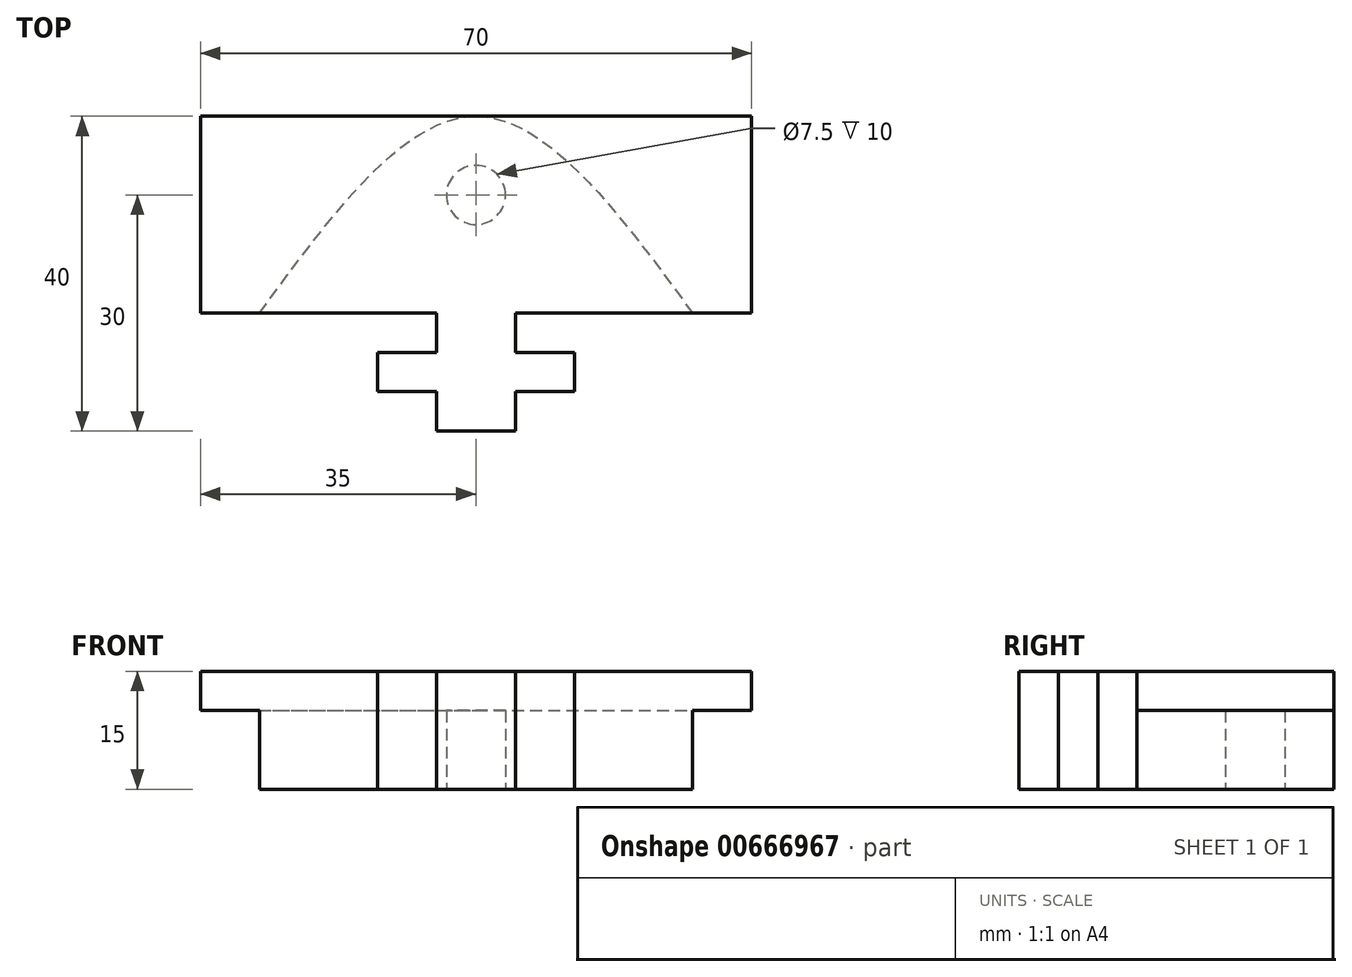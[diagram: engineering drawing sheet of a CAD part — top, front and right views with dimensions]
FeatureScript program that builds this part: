
annotation { "Feature Type Name" : "Feature", "Feature Type Description" : "" }
export const myFeature = defineFeature(function(context is Context, id is Id, definition is map)
    precondition{}
    {
        {
            var Q0;
            Q0=qCreatedBy(makeId("Top.planeOp"),FACE);
            var sketch = newSketch(context, id + "F0", { "sketchPlane" : qUnion([Q0])});
            skLineSegment(sketch, "E0.bottom", {"start": v(-35, 12.5) * mm, "end": v(35, 12.5) * mm});
            skLineSegment(sketch, "E0.top", {"start": v(-35, -12.5) * mm, "end": v(-5, -12.5) * mm});
            skLineSegment(sketch, "E0.left", {"start": v(-35, 12.5) * mm, "end": v(-35, -12.5) * mm});
            skLineSegment(sketch, "E0.right", {"start": v(35, 12.5) * mm, "end": v(35, -12.5) * mm});
            skPoint(sketch, "E0.middle", {"position": v(0, 0) * mm});
            skLineSegment(sketch, "E1", {"start": v(0, -27.5) * mm, "end": v(0, -58.53) * mm, "construction": true});
            skLineSegment(sketch, "E2", {"start": v(-5, -12.5) * mm, "end": v(-5, -17.5) * mm});
            skLineSegment(sketch, "E3", {"start": v(-5, -17.5) * mm, "end": v(-12.5, -17.5) * mm});
            skLineSegment(sketch, "E4", {"start": v(-12.5, -17.5) * mm, "end": v(-12.5, -22.5) * mm});
            skLineSegment(sketch, "E5", {"start": v(-12.5, -22.5) * mm, "end": v(-5, -22.5) * mm});
            skLineSegment(sketch, "E6", {"start": v(-5, -22.5) * mm, "end": v(-5, -27.5) * mm});
            skLineSegment(sketch, "E7", {"start": v(-5, -27.5) * mm, "end": v(0, -27.5) * mm});
            skLineSegment(sketch, "E8.MirrorCS", {"start": v(5, -17.5) * mm, "end": v(12.5, -17.5) * mm});
            skLineSegment(sketch, "E9.MirrorCS", {"start": v(5, -12.5) * mm, "end": v(5, -17.5) * mm});
            skLineSegment(sketch, "E10.MirrorCS", {"start": v(12.5, -17.5) * mm, "end": v(12.5, -22.5) * mm});
            skLineSegment(sketch, "E11.MirrorCS", {"start": v(12.5, -22.5) * mm, "end": v(5, -22.5) * mm});
            skLineSegment(sketch, "E12.MirrorCS", {"start": v(5, -22.5) * mm, "end": v(5, -27.5) * mm});
            skLineSegment(sketch, "E13.MirrorCS", {"start": v(5, -27.5) * mm, "end": v(0, -27.5) * mm});
            skLineSegment(sketch, "E14.trimOffspring", {"start": v(5, -12.5) * mm, "end": v(35, -12.5) * mm});
            skLineSegment(sketch, "E15", {"start": v(0, 12.5) * mm, "end": v(0, -27.5) * mm, "construction": true});
            skPoint(sketch, "E16", {"position": v(0, 2.5) * mm});
            skPoint(sketch, "E17", {"position": v(-27.5, -12.5) * mm});
            skPoint(sketch, "E18", {"position": v(27.5, -12.5) * mm});
            skFitSpline(sketch, "E19", {"points": [v(-27.5, -12.5) * mm, v(0, 12.5) * mm, v(27.5, -12.5) * mm], "startDerivative": vector(55, 75) * mm, "endDerivative": vector(55, -75) * mm});
            skLineSegment(sketch, "E20", {"start": v(5, -12.5) * mm, "end": v(-5, -12.5) * mm});
            skCircle(sketch, "E21", {"center": v(0, 2.5) * mm, "radius": 3.75 * mm});
            skSolve(sketch);
        }
        {
            var Q0;
            {var subQ0=sQuery(id+"F0.wireOp",EDGE,"E0.right");Q0=makeQuery(id+"F0.imprint","IMPRINT",FACE,{"disambiguationData":[TD([[makeQuery(id+"F0.imprint","IMPRINT",EDGE,{"derivedFrom":subQ0}),-1.0]])]});}
            var Q1;
            {var subQ0=sQuery(id+"F0.wireOp",EDGE,"E0.left");Q1=makeQuery(id+"F0.imprint","IMPRINT",FACE,{"disambiguationData":[TD([[makeQuery(id+"F0.imprint","IMPRINT",EDGE,{"derivedFrom":subQ0}),1.0]])]});}
            var Q2;
            {var subQ6=sQuery(id+"F0.wireOp",EDGE,"E20");Q2=makeQuery(id+"F0.imprint","IMPRINT",FACE,{"disambiguationData":[TD([[makeQuery(id+"F0.imprint","IMPRINT",EDGE,{"derivedFrom":subQ6}),-1.0]])]});}
            var Q3;
            Q3=makeQuery(id+"F0.imprint","IMPRINT",FACE,{"disambiguationData":[TD([[makeQuery(id+"F0.imprint","IMPRINT",EDGE,{"derivedFrom":sQuery(id+"F0.wireOp",EDGE,"E2")}),1.0]])]});
            extrude(context, id + "F1", {"entities" : qUnion([Q0, Q1, Q2, Q3]), "depth" : 5 * mm, "offsetDistance" : 25 * mm});
        }
        {
            var Q0;
            {var subQ6=sQuery(id+"F0.wireOp",EDGE,"E20");Q0=makeQuery(id+"F0.imprint","IMPRINT",FACE,{"disambiguationData":[TD([[makeQuery(id+"F0.imprint","IMPRINT",EDGE,{"derivedFrom":subQ6}),-1.0]])]});}
            var Q1;
            Q1=makeQuery(id+"F0.imprint","IMPRINT",FACE,{"disambiguationData":[TD([[makeQuery(id+"F0.imprint","IMPRINT",EDGE,{"derivedFrom":sQuery(id+"F0.wireOp",EDGE,"E2")}),1.0]])]});
            extrude(context, id + "F2", {"entities" : qUnion([Q0, Q1]), "operationType" : NewBodyOperationType.ADD, "oppositeDirection" : true, "depth" : 10 * mm, "offsetDistance" : 25 * mm});
        }
        {
            var Q0;
            Q0=makeQuery(id+"F0.imprint","IMPRINT",FACE,{"disambiguationData":[TD([[makeQuery(id+"F0.imprint","IMPRINT",EDGE,{"derivedFrom":sQuery(id+"F0.wireOp",EDGE,"E21")}),1.0]])]});
            extrude(context, id + "F3", {"entities" : qUnion([Q0]), "operationType" : NewBodyOperationType.ADD, "depth" : 5 * mm, "offsetDistance" : 25 * mm});
        }
    });
